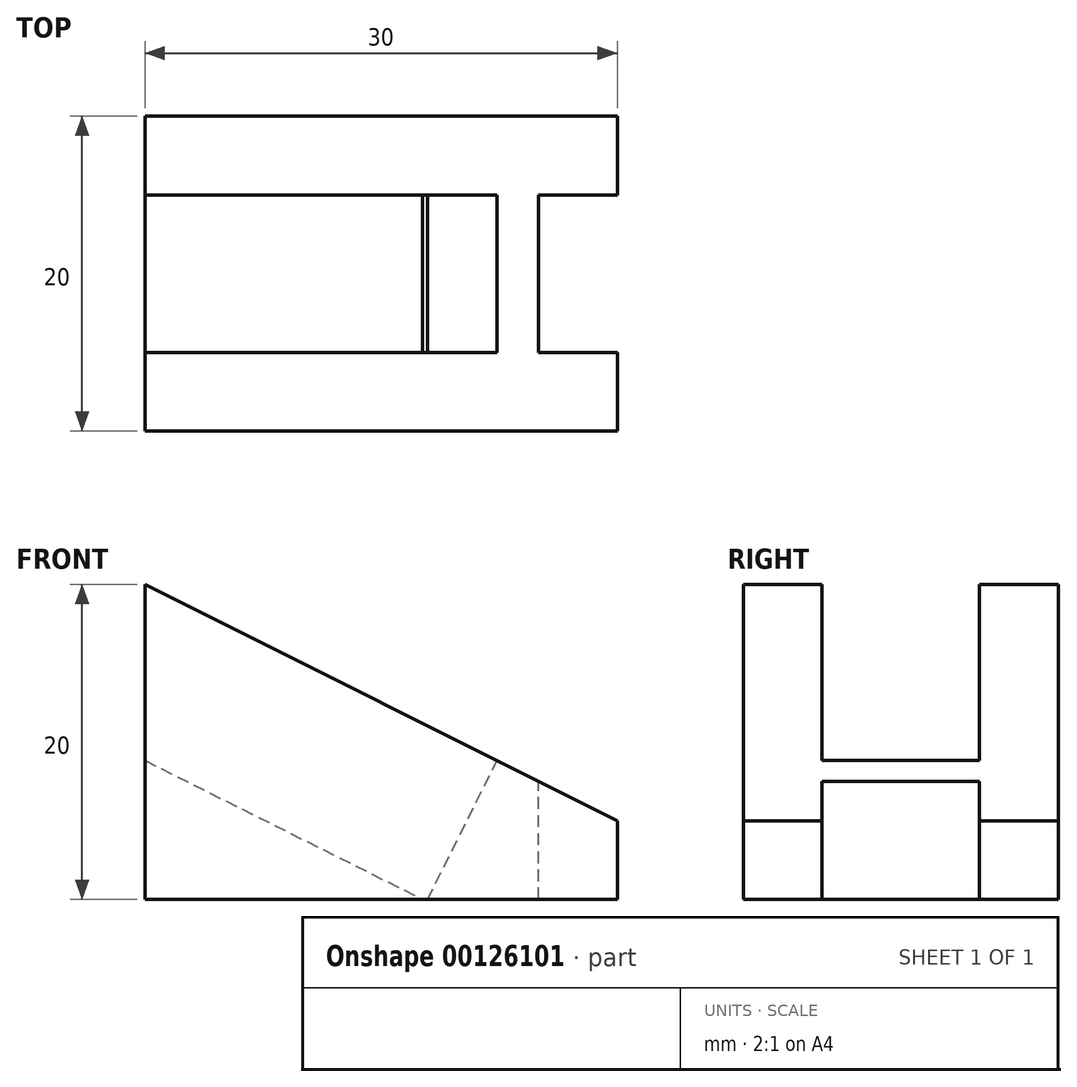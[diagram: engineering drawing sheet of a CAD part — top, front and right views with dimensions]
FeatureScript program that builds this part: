
annotation { "Feature Type Name" : "Feature", "Feature Type Description" : "" }
export const myFeature = defineFeature(function(context is Context, id is Id, definition is map)
    precondition{}
    {
        {
            var Q0;
            Q0=qCreatedBy(makeId("Front.planeOp"),FACE);
            var sketch = newSketch(context, id + "F0", { "sketchPlane" : qUnion([Q0])});
            skLineSegment(sketch, "E0", {"start": v(0, 20) * mm, "end": v(0, 0) * mm});
            skLineSegment(sketch, "E1", {"start": v(0, 0) * mm, "end": v(30, 0) * mm});
            skLineSegment(sketch, "E2", {"start": v(30, 0) * mm, "end": v(30, 5) * mm});
            skLineSegment(sketch, "E3", {"start": v(30, 5) * mm, "end": v(0, 20) * mm});
            skSolve(sketch);
        }
        {
            var Q0;
            Q0 = qSketchRegion(id + "F0", true);
            extrude(context, id + "F1", {"entities" : qUnion([Q0]), "oppositeDirection" : true, "depth" : 20 * mm});
        }
        {
            var Q0;
            Q0=makeQuery(id+"F1.opExtrude","SWEPT_FACE",FACE,{"disambiguationData":[OSD([sQuery(id+"F0.wireOp",EDGE,"E3")])]});
            var sketch = newSketch(context, id + "F2", { "sketchPlane" : qUnion([Q0])});
            skLineSegment(sketch, "E4", {"start": v(-8.94, 5) * mm, "end": v(16.06, 5) * mm});
            skLineSegment(sketch, "E5", {"start": v(16.06, 5) * mm, "end": v(16.06, 15) * mm});
            skLineSegment(sketch, "E6", {"start": v(16.06, 15) * mm, "end": v(-8.94, 15) * mm});
            skLineSegment(sketch, "E7", {"start": v(-8.94, 15) * mm, "end": v(-8.94, 5) * mm});
            skSolve(sketch);
        }
        {
            var Q0;
            Q0 = qSketchRegion(id + "F2", true);
            extrude(context, id + "F3", {"entities" : qUnion([Q0]), "operationType" : NewBodyOperationType.REMOVE, "oppositeDirection" : true, "depth" : 10 * mm});
        }
        {
            var Q0;
            Q0=makeQuery(id+"F1.opExtrude","SWEPT_FACE",FACE,{"disambiguationData":[OSD([sQuery(id+"F0.wireOp",EDGE,"E2")])]});
            var sketch = newSketch(context, id + "F4", { "sketchPlane" : qUnion([Q0])});
            skLineSegment(sketch, "E8", {"start": v(15, 0) * mm, "end": v(15, 7.5) * mm});
            skLineSegment(sketch, "E9", {"start": v(15, 7.5) * mm, "end": v(5, 7.5) * mm});
            skLineSegment(sketch, "E10", {"start": v(5, 7.5) * mm, "end": v(5, 0) * mm});
            skSolve(sketch);
        }
        {
            var Q0;
            {var subQ0=sQuery(id+"F4.wireOp",EDGE,"E8");var subQ1=sQuery(id+"F0.wireOp",EDGE,"E2");var subQ2=makeQuery(id+"F1.opExtrude","SWEPT_EDGE",EDGE,{"disambiguationData":[OSD([sQuery(id+"F0.wireOp",EDGE,"E1"),subQ1])]});var subQ3=makeQuery(id+"F4.imprint","INTERSECT",VERTEX,{"derivedFrom":[subQ2,subQ0]});Q0=makeQuery(id+"F4.imprint","IMPRINT",FACE,{"disambiguationData":[TD([[makeQuery(id+"F4.imprint","IMPRINT",EDGE,{"disambiguationData":[TD([[subQ3,-1.0]])],"derivedFrom":subQ0}),1.0]])]});}
            var Q1;
            {var subQ0=sQuery(id+"F4.wireOp",EDGE,"E9");Q1=makeQuery(id+"F4.imprint","IMPRINT",FACE,{"disambiguationData":[TD([[makeQuery(id+"F4.imprint","IMPRINT",EDGE,{"derivedFrom":subQ0}),1.0]])]});}
            extrude(context, id + "F5", {"entities" : qUnion([Q0, Q1]), "operationType" : NewBodyOperationType.REMOVE, "oppositeDirection" : true, "depth" : 5 * mm});
        }
    });
